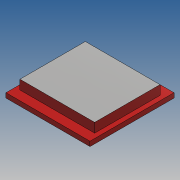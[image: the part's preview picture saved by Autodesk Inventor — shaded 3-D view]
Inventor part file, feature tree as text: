
AUTODESK INVENTOR PART (.ipt)
format: ipt  version: 2017 (Build 210142000, 142)  size: 95,744 bytes
history: native  units: mm
features: extrude x2, other x1, sketch x1
ambient origin geometry x8: Origin, YZ Plane, XZ Plane, XY Plane, X Axis, Y Axis, Z Axis, Center Point
bodies: Body1 (feature_tree)
feature tree (4):
  other  "Sólido1"
  sketch  "Boceto1"  dims[d0=45.0mm d1=45.0mm d2=35.0mm d3=40.0mm d4=2.5mm d5=0.0mm d6=5.0mm d7=0.0mm]
  extrude  "Extrusión1"  Depth=45.0mm
  extrude  "Extrusión2"  Depth=35.0mm
